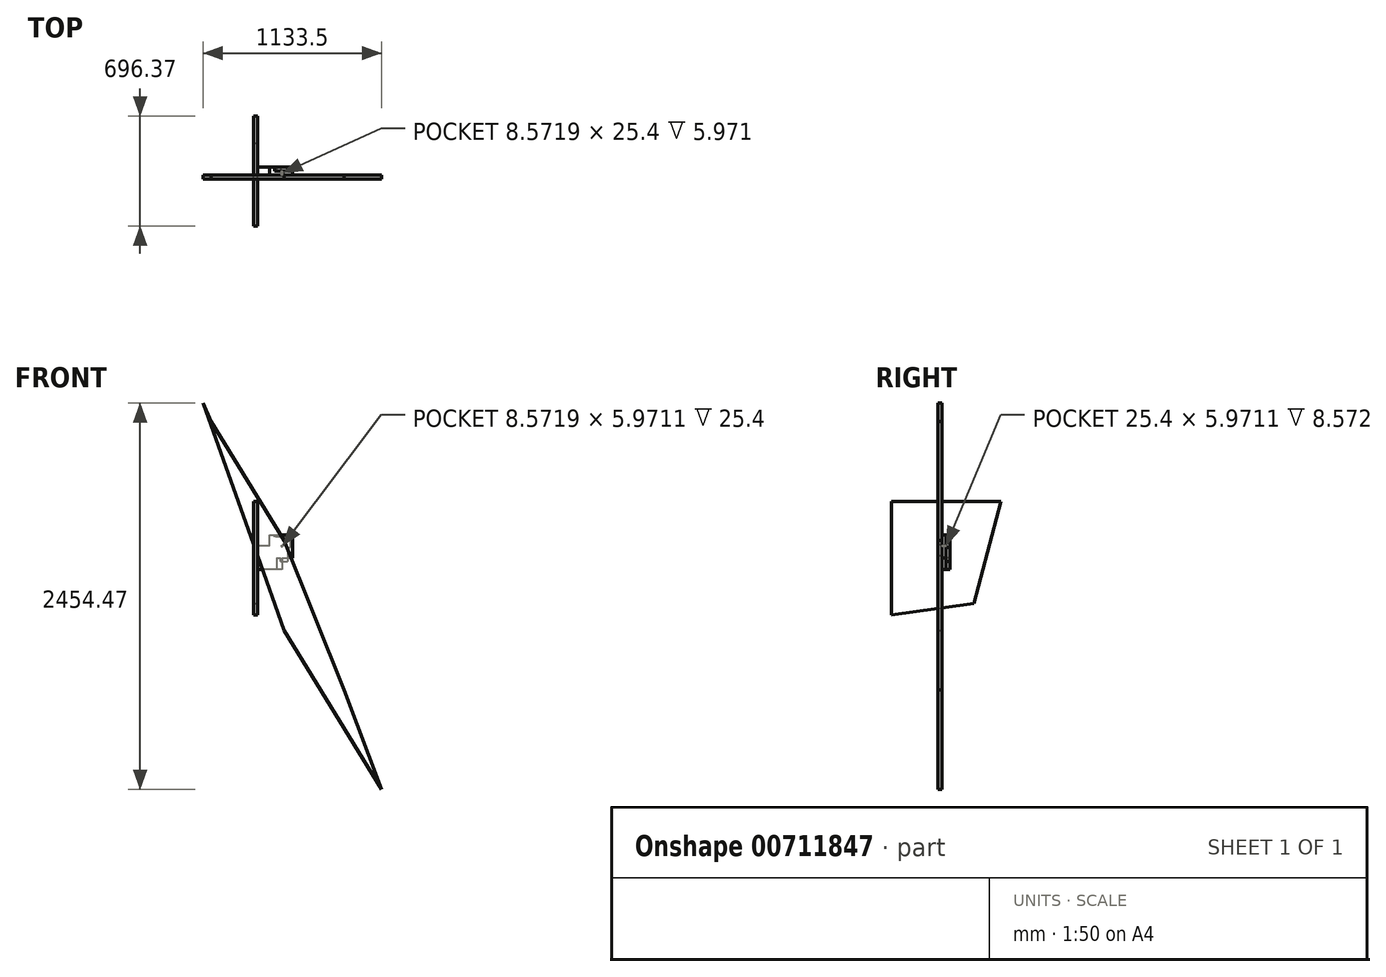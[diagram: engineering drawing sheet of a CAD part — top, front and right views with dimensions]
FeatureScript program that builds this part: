
annotation { "Feature Type Name" : "Feature", "Feature Type Description" : "" }
export const myFeature = defineFeature(function(context is Context, id is Id, definition is map)
    precondition{}
    {
        {
            var Q0;
            Q0=qCreatedBy(makeId("Front.planeOp"),FACE);
            var sketch = newSketch(context, id + "F0", { "sketchPlane" : qUnion([Q0])});
            skLineSegment(sketch, "E0", {"start": v(-386.4, 888.18) * mm, "end": v(90.7, 111.33) * mm});
            skLineSegment(sketch, "E1", {"start": v(90.7, 111.33) * mm, "end": v(473.22, -839.54) * mm});
            skLineSegment(sketch, "E2", {"start": v(473.22, -839.54) * mm, "end": v(710.13, -1470.77) * mm});
            skLineSegment(sketch, "E3", {"start": v(710.13, -1470.77) * mm, "end": v(92.5, -462.1) * mm});
            skLineSegment(sketch, "E4", {"start": v(92.5, -462.1) * mm, "end": v(-423.37, 983.7) * mm});
            skLineSegment(sketch, "E5", {"start": v(-423.37, 983.7) * mm, "end": v(149.87, -355.9) * mm});
            skLineSegment(sketch, "E6", {"start": v(149.87, -355.9) * mm, "end": v(-423.37, 983.7) * mm});
            skSolve(sketch);
        }
        {
            var Q0;
            Q0 = qSketchRegion(id + "F0", true);
            extrude(context, id + "F1", {"entities" : qUnion([Q0]), "depth" : 25.4 * mm, "offsetDistance" : 25.4 * mm});
        }
        {
            var Q0;
            Q0=makeQuery(id+"F1.opExtrude","CAP_FACE",FACE,{"disambiguationData":[OSD([sQuery(id+"F0.wireOp",EDGE,"E0"),sQuery(id+"F0.wireOp",EDGE,"E1"),sQuery(id+"F0.wireOp",EDGE,"E2"),sQuery(id+"F0.wireOp",EDGE,"E3"),sQuery(id+"F0.wireOp",EDGE,"E4"),sQuery(id+"F0.wireOp",EDGE,"E6")])],"isStart":true});
            var sketch = newSketch(context, id + "F2", { "sketchPlane" : qUnion([Q0])});
            skLineSegment(sketch, "E7.bottom", {"start": v(-73.33, 78.37) * mm, "end": v(-81.9, 78.37) * mm});
            skLineSegment(sketch, "E7.top", {"start": v(-73.33, 72.4) * mm, "end": v(-81.9, 72.4) * mm});
            skLineSegment(sketch, "E7.left", {"start": v(-73.33, 78.37) * mm, "end": v(-73.33, 72.4) * mm});
            skLineSegment(sketch, "E7.right", {"start": v(-81.9, 78.37) * mm, "end": v(-81.9, 72.4) * mm});
            skPoint(sketch, "E7.middle", {"position": v(-77.62, 75.38) * mm});
            skLineSegment(sketch, "E8.bottom", {"start": v(0, 0) * mm, "end": v(-146.67, 0) * mm});
            skLineSegment(sketch, "E8.top", {"start": v(0, 144.8) * mm, "end": v(-146.67, 144.8) * mm});
            skLineSegment(sketch, "E8.left", {"start": v(0, 0) * mm, "end": v(0, 144.8) * mm});
            skLineSegment(sketch, "E8.right", {"start": v(-146.67, 0) * mm, "end": v(-146.67, 144.8) * mm});
            skPoint(sketch, "E8.middle", {"position": v(-73.33, 72.4) * mm});
            skLineSegment(sketch, "E9.bottom", {"start": v(-77.62, 75.38) * mm, "end": v(77.62, 75.38) * mm});
            skLineSegment(sketch, "E9.top", {"start": v(-77.62, -75.38) * mm, "end": v(77.62, -75.38) * mm});
            skLineSegment(sketch, "E9.left", {"start": v(-77.62, 75.38) * mm, "end": v(-77.62, -75.38) * mm});
            skLineSegment(sketch, "E9.right", {"start": v(77.62, 75.38) * mm, "end": v(77.62, -75.38) * mm});
            skPoint(sketch, "E9.middle", {"position": v(0, 0) * mm});
            skSolve(sketch);
        }
        {
            var Q0;
            Q0 = qSketchRegion(id + "F2", true);
            extrude(context, id + "F3", {"entities" : qUnion([Q0]), "operationType" : NewBodyOperationType.ADD, "depth" : 25.4 * mm, "offsetDistance" : 25.4 * mm});
        }
        {
            var Q0;
            Q0=makeQuery(id+"F3.opExtrude","CAP_FACE",FACE,{"disambiguationData":[OSD([sQuery(id+"F2.wireOp",EDGE,"E7.bottom"),sQuery(id+"F2.wireOp",EDGE,"E7.top"),sQuery(id+"F2.wireOp",EDGE,"E7.left"),sQuery(id+"F2.wireOp",EDGE,"E7.right"),sQuery(id+"F2.wireOp",EDGE,"E8.bottom"),sQuery(id+"F2.wireOp",EDGE,"E8.top"),sQuery(id+"F2.wireOp",EDGE,"E8.left"),sQuery(id+"F2.wireOp",EDGE,"E8.right"),sQuery(id+"F2.wireOp",EDGE,"E9.bottom"),sQuery(id+"F2.wireOp",EDGE,"E9.top"),sQuery(id+"F2.wireOp",EDGE,"E9.left"),sQuery(id+"F2.wireOp",EDGE,"E9.right")])],"isStart":false});
            var sketch = newSketch(context, id + "F4", { "sketchPlane" : qUnion([Q0])});
            skLineSegment(sketch, "E10.bottom", {"start": v(-29.75, 64.66) * mm, "end": v(0, 64.66) * mm});
            skLineSegment(sketch, "E10.top", {"start": v(-29.75, 144.8) * mm, "end": v(0, 144.8) * mm});
            skLineSegment(sketch, "E10.left", {"start": v(-29.75, 64.66) * mm, "end": v(-29.75, 144.8) * mm});
            skLineSegment(sketch, "E10.right", {"start": v(0, 64.66) * mm, "end": v(0, 144.8) * mm});
            skLineSegment(sketch, "E11.bottom", {"start": v(-29.75, 64.66) * mm, "end": v(77.62, 64.66) * mm});
            skLineSegment(sketch, "E11.top", {"start": v(-29.75, 75.38) * mm, "end": v(77.62, 75.38) * mm});
            skLineSegment(sketch, "E11.left", {"start": v(-29.75, 64.66) * mm, "end": v(-29.75, 75.38) * mm});
            skLineSegment(sketch, "E11.right", {"start": v(77.62, 64.66) * mm, "end": v(77.62, 75.38) * mm});
            skLineSegment(sketch, "E12.bottom", {"start": v(-43.3, 64.66) * mm, "end": v(77.62, 64.66) * mm});
            skLineSegment(sketch, "E12.top", {"start": v(-43.3, -75.38) * mm, "end": v(77.62, -75.38) * mm});
            skLineSegment(sketch, "E12.left", {"start": v(-43.3, 64.66) * mm, "end": v(-43.3, -75.38) * mm});
            skLineSegment(sketch, "E12.right", {"start": v(77.62, 64.66) * mm, "end": v(77.62, -75.38) * mm});
            skLineSegment(sketch, "E13.bottom", {"start": v(-43.3, 64.66) * mm, "end": v(-112.14, 64.66) * mm});
            skLineSegment(sketch, "E13.top", {"start": v(-43.3, 0) * mm, "end": v(-112.14, 0) * mm});
            skLineSegment(sketch, "E13.left", {"start": v(-43.3, 64.66) * mm, "end": v(-43.3, 0) * mm});
            skLineSegment(sketch, "E13.right", {"start": v(-112.14, 64.66) * mm, "end": v(-112.14, 0) * mm});
            skLineSegment(sketch, "E14.bottom", {"start": v(-69.09, -22.18) * mm, "end": v(-112.14, -22.18) * mm});
            skLineSegment(sketch, "E14.top", {"start": v(-69.09, 64.66) * mm, "end": v(-112.14, 64.66) * mm});
            skLineSegment(sketch, "E14.left", {"start": v(-69.09, -22.18) * mm, "end": v(-69.09, 64.66) * mm});
            skLineSegment(sketch, "E14.right", {"start": v(-112.14, -22.18) * mm, "end": v(-112.14, 64.66) * mm});
            skLineSegment(sketch, "E15.bottom", {"start": v(-112.14, 64.66) * mm, "end": v(-130.15, 64.66) * mm});
            skLineSegment(sketch, "E15.top", {"start": v(-112.14, 116.26) * mm, "end": v(-130.15, 116.26) * mm});
            skLineSegment(sketch, "E15.left", {"start": v(-112.14, 64.66) * mm, "end": v(-112.14, 116.26) * mm});
            skLineSegment(sketch, "E15.right", {"start": v(-130.15, 64.66) * mm, "end": v(-130.15, 116.26) * mm});
            skLineSegment(sketch, "E16.bottom", {"start": v(-128.12, 118.62) * mm, "end": v(-130.15, 118.62) * mm});
            skLineSegment(sketch, "E16.top", {"start": v(-128.12, 116.26) * mm, "end": v(-130.15, 116.26) * mm});
            skLineSegment(sketch, "E16.left", {"start": v(-128.12, 118.62) * mm, "end": v(-128.12, 116.26) * mm});
            skLineSegment(sketch, "E16.right", {"start": v(-130.15, 118.62) * mm, "end": v(-130.15, 116.26) * mm});
            skLineSegment(sketch, "E17.bottom", {"start": v(-112.14, 116.26) * mm, "end": v(-29.75, 116.26) * mm});
            skLineSegment(sketch, "E17.top", {"start": v(-112.14, 132) * mm, "end": v(-29.75, 132) * mm});
            skLineSegment(sketch, "E17.left", {"start": v(-112.14, 116.26) * mm, "end": v(-112.14, 132) * mm});
            skLineSegment(sketch, "E17.right", {"start": v(-29.75, 116.26) * mm, "end": v(-29.75, 132) * mm});
            skSolve(sketch);
        }
        {
            var Q0;
            Q0 = qSketchRegion(id + "F4", true);
            extrude(context, id + "F5", {"entities" : qUnion([Q0]), "operationType" : NewBodyOperationType.ADD, "depth" : 25.4 * mm, "offsetDistance" : 25.4 * mm});
        }
        {
            var Q0;
            Q0=makeQuery(id+"F5.boolean.opBoolean","MERGE",FACE,{"derivedFrom":[makeQuery(id+"F3.opExtrude","SWEPT_FACE",FACE,{"disambiguationData":[OSD([sQuery(id+"F2.wireOp",EDGE,"E9.right")])]}),makeQuery(id+"F5.opExtrude","SWEPT_FACE",FACE,{"disambiguationData":[OSD([sQuery(id+"F4.wireOp",EDGE,"E11.right"),sQuery(id+"F4.wireOp",EDGE,"E12.right")])]})]});
            var sketch = newSketch(context, id + "F6", { "sketchPlane" : qUnion([Q0])});
            skLineSegment(sketch, "E18", {"start": v(-374.67, 356.46) * mm, "end": v(321.7, 356.46) * mm});
            skLineSegment(sketch, "E19", {"start": v(321.7, 356.46) * mm, "end": v(321.7, -362.34) * mm});
            skLineSegment(sketch, "E20", {"start": v(321.7, -362.34) * mm, "end": v(-204.55, -290.01) * mm});
            skLineSegment(sketch, "E21", {"start": v(-204.55, -290.01) * mm, "end": v(-374.67, 356.46) * mm});
            skSolve(sketch);
        }
        {
            var Q0;
            Q0 = qSketchRegion(id + "F6", true);
            extrude(context, id + "F7", {"entities" : qUnion([Q0]), "operationType" : NewBodyOperationType.ADD, "depth" : 25.4 * mm, "offsetDistance" : 25.4 * mm});
        }
    });
